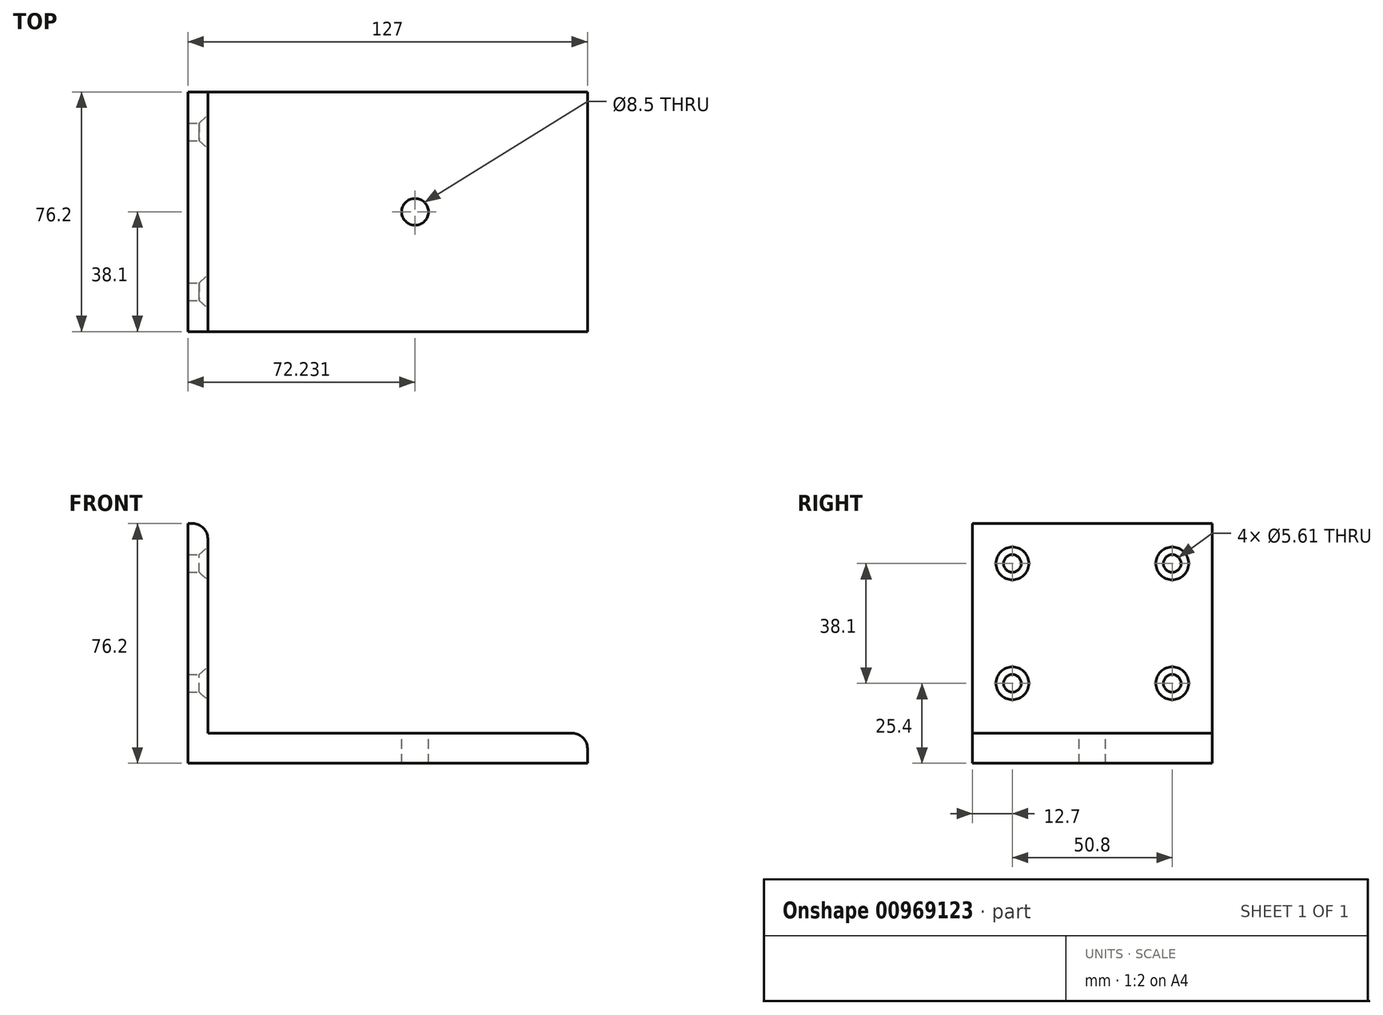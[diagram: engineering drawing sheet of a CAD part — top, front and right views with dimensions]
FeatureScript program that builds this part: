
annotation { "Feature Type Name" : "Feature", "Feature Type Description" : "" }
export const myFeature = defineFeature(function(context is Context, id is Id, definition is map)
    precondition{}
    {
        {
            var Q0;
            Q0=qCreatedBy(makeId("Front.planeOp"),FACE);
            var sketch = newSketch(context, id + "F0", { "sketchPlane" : qUnion([Q0])});
            skLineSegment(sketch, "E0", {"start": v(0, 0) * mm, "end": v(0, 76.2) * mm});
            skLineSegment(sketch, "E1", {"start": v(0, 76.2) * mm, "end": v(1.55, 76.2) * mm});
            skLineSegment(sketch, "E2", {"start": v(6.35, 71.4) * mm, "end": v(6.35, 9.52) * mm});
            skLineSegment(sketch, "E3", {"start": v(6.35, 9.52) * mm, "end": v(122.2, 9.53) * mm});
            skLineSegment(sketch, "E4", {"start": v(127, 4.73) * mm, "end": v(127, 0) * mm});
            skLineSegment(sketch, "E5", {"start": v(127, 0) * mm, "end": v(0, 0) * mm});
            skPoint(sketch, "E6.visualSharp", {"position": v(6.35, 76.2) * mm});
            skArc(sketch, "E6.filletArc", {"start": v(6.35, 71.4) * mm, "mid": v(4.94, 74.8) * mm, "end": v(1.55, 76.2) * mm});
            skPoint(sketch, "E7.visualSharp", {"position": v(127, 9.53) * mm});
            skArc(sketch, "E7.filletArc", {"start": v(127, 4.73) * mm, "mid": v(125.6, 8.12) * mm, "end": v(122.2, 9.53) * mm});
            skSolve(sketch);
        }
        {
            var Q0;
            Q0 = qSketchRegion(id + "F0", true);
            extrude(context, id + "F1", {"entities" : qUnion([Q0]), "depth" : 76.2 * mm, "offsetDistance" : 25.4 * mm});
        }
        {
            var Q0;
            Q0=makeQuery(id+"F1.opExtrude","SWEPT_FACE",FACE,{"disambiguationData":[OSD([sQuery(id+"F0.wireOp",EDGE,"E3")])]});
            var sketch = newSketch(context, id + "F2", { "sketchPlane" : qUnion([Q0])});
            skPoint(sketch, "E8", {"position": v(72.23, -38.1) * mm});
            skSolve(sketch);
        }
        {
            var Q0;
            Q0=sQuery(id+"F2.wireOp",VERTEX,"E8");
            var Q1;
            Q1=makeQuery(id+"F1.opExtrude","SWEPT_BODY",BODY,{"disambiguationData":[OSD([sQuery(id+"F0.wireOp",EDGE,"E0"),sQuery(id+"F0.wireOp",EDGE,"E1"),sQuery(id+"F0.wireOp",EDGE,"E2"),sQuery(id+"F0.wireOp",EDGE,"E3"),sQuery(id+"F0.wireOp",EDGE,"E4"),sQuery(id+"F0.wireOp",EDGE,"E5"),sQuery(id+"F0.wireOp",EDGE,"E6.filletArc"),sQuery(id+"F0.wireOp",EDGE,"E7.filletArc")])]});
            hole(context, id + "F3", {"style" : HoleStyle.SIMPLE, "endStyle" : HoleEndStyle.THROUGH, "standardTappedOrClearance" : lookupTablePath({ "standard" : "ISO", "engagement" : "75%", "pitch" : "1.5 mm", "size" : "M10", "type" : "Tapped" }), "standardBlindInLast" : lookupTablePath({ "standard" : "ISO", "fit" : "Normal", "engagement" : "75%", "pitch" : "1.5 mm", "size" : "M10", "type" : "Clearance & tapped" }), "holeDiameter" : 8.5 * mm, "majorDiameter" : 10 * mm, "showTappedDepth" : true, "isTappedThrough" : true, "tappedDepth" : 12.7 * mm, "tapClearance" : 3, "locations" : qUnion([Q0]), "scope" : qUnion([Q1])});
        }
        {
            var Q0;
            Q0=makeQuery(id+"F1.opExtrude","SWEPT_FACE",FACE,{"disambiguationData":[OSD([sQuery(id+"F0.wireOp",EDGE,"E2")])]});
            var sketch = newSketch(context, id + "F4", { "sketchPlane" : qUnion([Q0])});
            skPoint(sketch, "E9", {"position": v(-63.5, 63.5) * mm});
            skPoint(sketch, "E10", {"position": v(-63.5, 25.4) * mm});
            skPoint(sketch, "E11", {"position": v(-12.7, 25.4) * mm});
            skPoint(sketch, "E12", {"position": v(-12.7, 63.5) * mm});
            skSolve(sketch);
        }
        {
            var Q0;
            Q0=sQuery(id+"F4.wireOp",VERTEX,"E9");
            var Q1;
            Q1=sQuery(id+"F4.wireOp",VERTEX,"E10");
            var Q2;
            Q2=sQuery(id+"F4.wireOp",VERTEX,"E11");
            var Q3;
            Q3=sQuery(id+"F4.wireOp",VERTEX,"E12");
            var Q4;
            Q4=makeQuery(id+"F1.opExtrude","SWEPT_BODY",BODY,{"disambiguationData":[OSD([sQuery(id+"F0.wireOp",EDGE,"E0"),sQuery(id+"F0.wireOp",EDGE,"E1"),sQuery(id+"F0.wireOp",EDGE,"E2"),sQuery(id+"F0.wireOp",EDGE,"E3"),sQuery(id+"F0.wireOp",EDGE,"E4"),sQuery(id+"F0.wireOp",EDGE,"E5"),sQuery(id+"F0.wireOp",EDGE,"E6.filletArc"),sQuery(id+"F0.wireOp",EDGE,"E7.filletArc")])]});
            hole(context, id + "F5", {"style" : HoleStyle.C_SINK, "endStyle" : HoleEndStyle.THROUGH, "standardTappedOrClearance" : lookupTablePath({ "fit" : "Normal (ASME)", "standard" : "ANSI", "size" : "#10", "type" : "Clearance" }), "standardBlindInLast" : lookupTablePath({ "fit" : "Normal", "standard" : "ANSI", "engagement" : "75%", "pitch" : "24 tpi", "size" : "#10", "type" : "Clearance & tapped" }), "holeDiameter" : 5.61 * mm, "cSinkDiameter" : 10.44 * mm, "cSinkAngle" : 82 * degree, "majorDiameter" : 9.52 * mm, "isTappedThrough" : true, "tappedDepth" : 12.7 * mm, "tapClearance" : 3, "locations" : qUnion([Q0, Q1, Q2, Q3]), "scope" : qUnion([Q4])});
        }
    });
